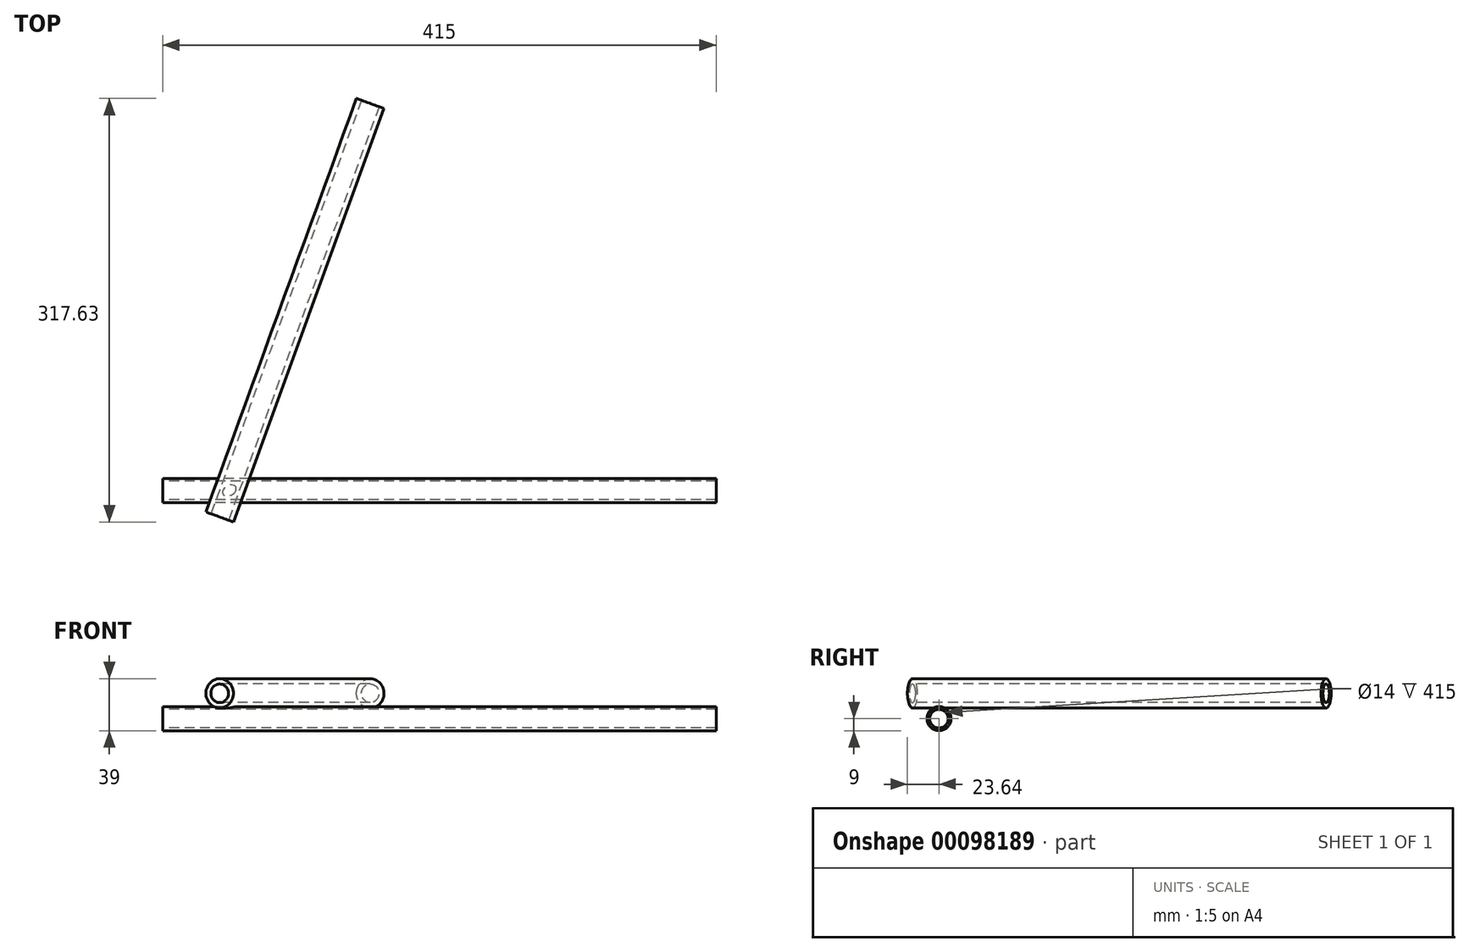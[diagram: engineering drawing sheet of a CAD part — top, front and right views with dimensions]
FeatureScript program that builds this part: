
annotation { "Feature Type Name" : "Feature", "Feature Type Description" : "" }
export const myFeature = defineFeature(function(context is Context, id is Id, definition is map)
    precondition{}
    {
        {
            var Q0;
            Q0=qCreatedBy(makeId("Right.planeOp"),FACE);
            var sketch = newSketch(context, id + "F0", { "sketchPlane" : qUnion([Q0])});
            skCircle(sketch, "E0", {"center": v(0, 0) * mm, "radius": 9 * mm});
            skCircle(sketch, "E1", {"center": v(0, 0) * mm, "radius": 7 * mm});
            skSolve(sketch);
        }
        {
            var Q0;
            Q0=makeQuery(id+"F0.imprint","IMPRINT",FACE,{"disambiguationData":[TD([[makeQuery(id+"F0.imprint","IMPRINT",EDGE,{"derivedFrom":sQuery(id+"F0.wireOp",EDGE,"E0")}),1.0]])]});
            extrude(context, id + "F1", {"entities" : qUnion([Q0]), "depth" : 415 * mm});
        }
        {
            var Q0;
            Q0=qCreatedBy(makeId("Top.planeOp"),FACE);
            var sketch = newSketch(context, id + "F2", { "sketchPlane" : qUnion([Q0])});
            skLineSegment(sketch, "E2", {"start": v(50, 0) * mm, "end": v(93.68, 120) * mm, "construction": true});
            skSolve(sketch);
        }
        {
            var Q0;
            Q0=sQuery(id+"F2.wireOp",EDGE,"E2");
            cPlane(context, id + "F3", {"entities" : qUnion([Q0]), "cplaneType" : CPlaneType.MID_PLANE, "offset" : 150 * mm, "width" : 150 * mm, "height" : 150 * mm});
        }
        {
            var Q0;
            Q0=qCreatedBy(id+"F3.planeOp",FACE);
            cPlane(context, id + "F4", {"entities" : qUnion([Q0]), "cplaneType" : CPlaneType.OFFSET, "offset" : 85 * mm, "oppositeDirection" : true, "width" : 150 * mm, "height" : 150 * mm});
        }
        {
            var Q0;
            Q0=qCreatedBy(id+"F4.planeOp",FACE);
            var sketch = newSketch(context, id + "F5", { "sketchPlane" : qUnion([Q0])});
            skCircle(sketch, "E3", {"center": v(-46.98, 19) * mm, "radius": 11 * mm});
            skCircle(sketch, "E4", {"center": v(-46.98, 19) * mm, "radius": 7 * mm});
            skSolve(sketch);
        }
        {
            var Q0;
            Q0=makeQuery(id+"F5.imprint","IMPRINT",FACE,{"disambiguationData":[TD([[makeQuery(id+"F5.imprint","IMPRINT",EDGE,{"derivedFrom":sQuery(id+"F5.wireOp",EDGE,"E3")}),1.0]])]});
            extrude(context, id + "F6", {"entities" : qUnion([Q0]), "operationType" : NewBodyOperationType.ADD, "depth" : 330 * mm});
        }
        {
            var Q0;
            Q0=makeQuery(id+"F6.opExtrude","CAP_FACE",FACE,{"disambiguationData":[OSD([sQuery(id+"F5.wireOp",EDGE,"E3"),sQuery(id+"F5.wireOp",EDGE,"E4")])],"isStart":true});
            var sketch = newSketch(context, id + "F7", { "sketchPlane" : qUnion([Q0])});
            skCircle(sketch, "E5", {"center": v(46.98, 19) * mm, "radius": 7 * mm});
            skSolve(sketch);
        }
        {
            var Q0;
            Q0=qSketchRegion(id+"F7",true);
            extrude(context, id + "F8", {"entities" : qUnion([Q0]), "operationType" : NewBodyOperationType.REMOVE, "endBound" : BoundingType.THROUGH_ALL, "oppositeDirection" : true, "depth" : 25 * mm});
        }
    });
